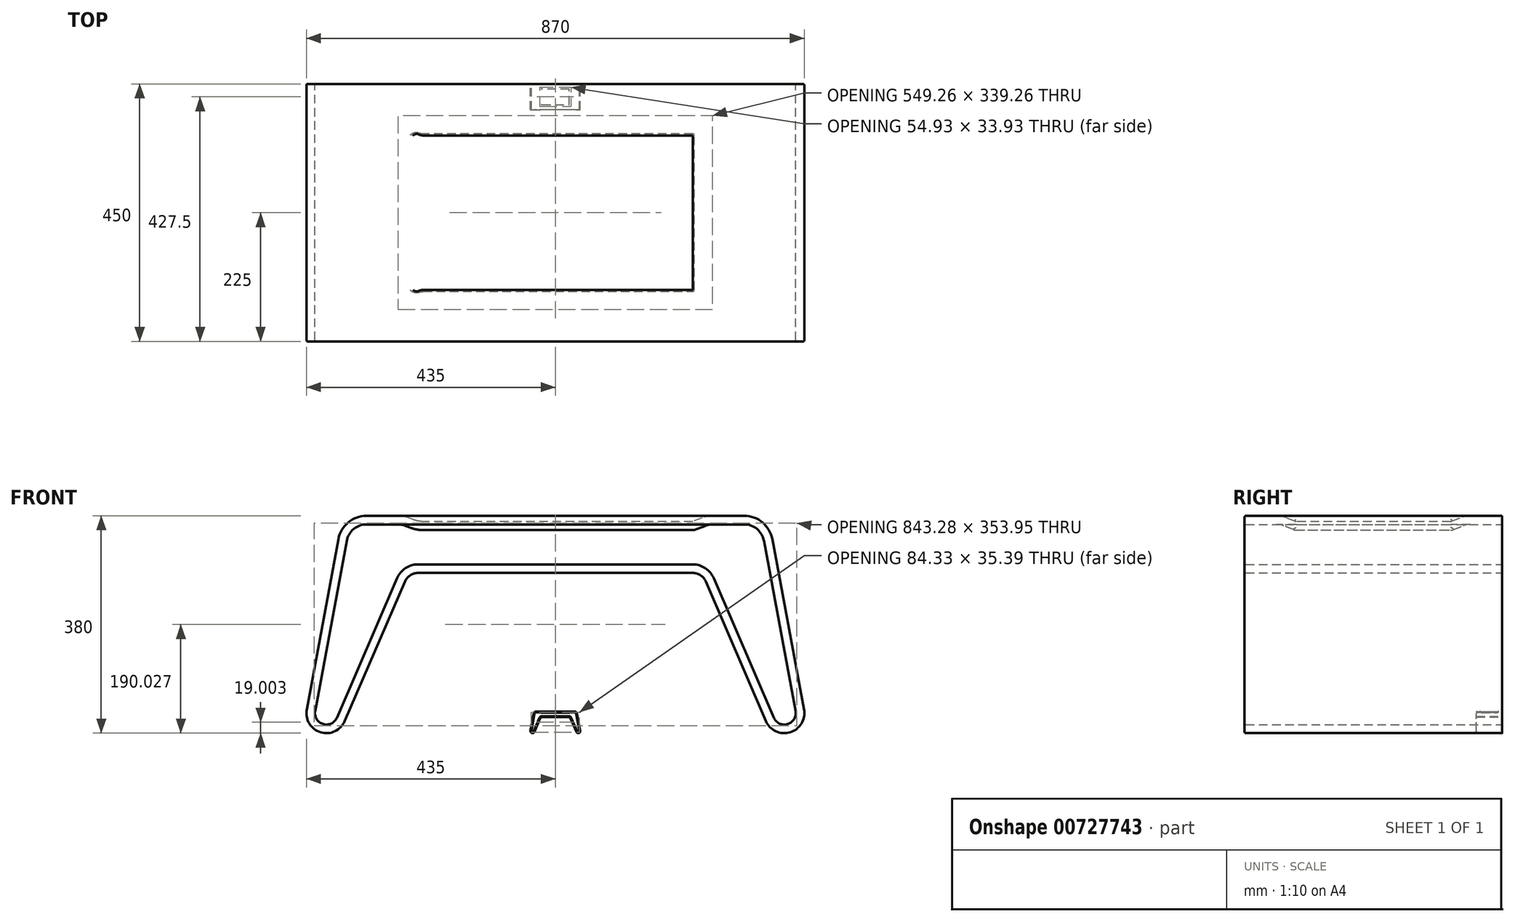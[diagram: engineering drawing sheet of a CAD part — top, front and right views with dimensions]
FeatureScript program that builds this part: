
annotation { "Feature Type Name" : "Feature", "Feature Type Description" : "" }
export const myFeature = defineFeature(function(context is Context, id is Id, definition is map)
    precondition{}
    {
        {
            var Q0;
            Q0=qCreatedBy(makeId("Front.planeOp"),FACE);
            var sketch = newSketch(context, id + "F0", { "sketchPlane" : qUnion([Q0])});
            skLineSegment(sketch, "E0", {"start": v(0, 0) * mm, "end": v(-40, 0) * mm, "construction": true});
            skLineSegment(sketch, "E1", {"start": v(0, 0) * mm, "end": v(0, 30) * mm, "construction": true});
            skArc(sketch, "E2", {"start": v(-43.44, 4.14) * mm, "mid": v(-41.02, 0.15) * mm, "end": v(-36.79, 2.12) * mm});
            skArc(sketch, "E3", {"start": v(-33, 38) * mm, "mid": v(-36.2, 36.84) * mm, "end": v(-37.92, 33.91) * mm});
            skLineSegment(sketch, "E4", {"start": v(0, 30) * mm, "end": v(0, 38) * mm, "construction": true});
            skLineSegment(sketch, "E5", {"start": v(0, 38) * mm, "end": v(-56.03, 38) * mm, "construction": true});
            skLineSegment(sketch, "E6", {"start": v(-43.44, 4.14) * mm, "end": v(-37.92, 33.91) * mm});
            skArc(sketch, "E7", {"start": v(-24, 28) * mm, "mid": v(-25.37, 27.59) * mm, "end": v(-26.3, 26.49) * mm});
            skLineSegment(sketch, "E8", {"start": v(-36.79, 2.12) * mm, "end": v(-26.3, 26.49) * mm});
            skLineSegment(sketch, "E9", {"start": v(0, 28) * mm, "end": v(-24, 28) * mm});
            skLineSegment(sketch, "E10", {"start": v(-33, 38) * mm, "end": v(0, 38) * mm});
            skLineSegment(sketch, "E11.MirrorCS", {"start": v(33, 38) * mm, "end": v(0, 38) * mm});
            skArc(sketch, "E12.MirrorCS", {"start": v(33, 38) * mm, "mid": v(36.2, 36.84) * mm, "end": v(37.92, 33.91) * mm});
            skLineSegment(sketch, "E13.MirrorCS", {"start": v(43.44, 4.14) * mm, "end": v(37.92, 33.91) * mm});
            skArc(sketch, "E14.MirrorCS", {"start": v(43.44, 4.14) * mm, "mid": v(41.02, 0.15) * mm, "end": v(36.79, 2.12) * mm});
            skLineSegment(sketch, "E15.MirrorCS", {"start": v(36.79, 2.12) * mm, "end": v(26.3, 26.49) * mm});
            skArc(sketch, "E16.MirrorCS", {"start": v(24, 28) * mm, "mid": v(25.37, 27.59) * mm, "end": v(26.3, 26.49) * mm});
            skLineSegment(sketch, "E17.MirrorCS", {"start": v(0, 28) * mm, "end": v(24, 28) * mm});
            skCircle(sketch, "E18", {"center": v(0, 11.76) * mm, "radius": 50 * mm, "construction": true});
            skSolve(sketch);
        }
        {
            var Q0;
            Q0=makeQuery(id+"F0.imprint","IMPRINT",FACE,{"disambiguationData":[TD([[makeQuery(id+"F0.imprint","IMPRINT",EDGE,{"derivedFrom":sQuery(id+"F0.wireOp",EDGE,"E2")}),1.0]])]});
            extrude(context, id + "F1", {"entities" : qUnion([Q0]), "depth" : 45 * mm, "offsetDistance" : 25 * mm});
        }
        {
            var Q0;
            Q0=makeQuery(id+"F1.opExtrude","SWEPT_FACE",FACE,{"disambiguationData":[OSD([sQuery(id+"F0.wireOp",EDGE,"E10"),sQuery(id+"F0.wireOp",EDGE,"E11.MirrorCS")])]});
            var sketch = newSketch(context, id + "F2", { "sketchPlane" : qUnion([Q0])});
            skLineSegment(sketch, "E19.0.0", {"start": v(33, 0) * mm, "end": v(-33, 0) * mm});
            skLineSegment(sketch, "E19.0.1", {"start": v(-33, 0) * mm, "end": v(-33, -45) * mm});
            skLineSegment(sketch, "E19.0.2", {"start": v(-33, -45) * mm, "end": v(33, -45) * mm});
            skLineSegment(sketch, "E19.0.3", {"start": v(33, -45) * mm, "end": v(33, 0) * mm});
            skLineSegment(sketch, "E20.0", {"start": v(-29, -9) * mm, "end": v(-29, -36) * mm});
            skLineSegment(sketch, "E20.1", {"start": v(24, -4) * mm, "end": v(-24, -4) * mm});
            skLineSegment(sketch, "E20.2", {"start": v(29, -36) * mm, "end": v(29, -9) * mm});
            skLineSegment(sketch, "E20.3", {"start": v(-24, -41) * mm, "end": v(24, -41) * mm});
            skPoint(sketch, "E21.visualSharp", {"position": v(-29, -4) * mm});
            skArc(sketch, "E21.filletArc", {"start": v(-24, -4) * mm, "mid": v(-27.54, -5.46) * mm, "end": v(-29, -9) * mm});
            skPoint(sketch, "E22.visualSharp", {"position": v(29, -4) * mm});
            skArc(sketch, "E22.filletArc", {"start": v(29, -9) * mm, "mid": v(27.54, -5.46) * mm, "end": v(24, -4) * mm});
            skPoint(sketch, "E23.visualSharp", {"position": v(29, -41) * mm});
            skArc(sketch, "E23.filletArc", {"start": v(24, -41) * mm, "mid": v(27.54, -39.54) * mm, "end": v(29, -36) * mm});
            skPoint(sketch, "E24.visualSharp", {"position": v(-29, -41) * mm});
            skArc(sketch, "E24.filletArc", {"start": v(-29, -36) * mm, "mid": v(-27.54, -39.54) * mm, "end": v(-24, -41) * mm});
            skSolve(sketch);
        }
        {
            var Q0;
            Q0=makeQuery(id+"F2.imprint","IMPRINT",FACE,{"disambiguationData":[TD([[makeQuery(id+"F2.imprint","IMPRINT",EDGE,{"derivedFrom":sQuery(id+"F2.wireOp",EDGE,"E20.0")}),1.0]])]});
            extrude(context, id + "F3", {"entities" : qUnion([Q0]), "operationType" : NewBodyOperationType.REMOVE, "oppositeDirection" : true, "depth" : 1 * mm, "offsetDistance" : 25 * mm});
        }
        {
            var Q0;
            Q0=makeQuery(id+"F3.boolean.opBoolean","COPY",FACE,{"derivedFrom":makeQuery(id+"F3.opExtrude","CAP_FACE",FACE,{"disambiguationData":[OSD([sQuery(id+"F2.wireOp",EDGE,"E20.0"),sQuery(id+"F2.wireOp",EDGE,"E20.1"),sQuery(id+"F2.wireOp",EDGE,"E20.2"),sQuery(id+"F2.wireOp",EDGE,"E20.3"),sQuery(id+"F2.wireOp",EDGE,"E21.filletArc"),sQuery(id+"F2.wireOp",EDGE,"E22.filletArc"),sQuery(id+"F2.wireOp",EDGE,"E23.filletArc"),sQuery(id+"F2.wireOp",EDGE,"E24.filletArc")])],"isStart":false})});
            chamfer(context, id + "F4", {"entities" : qUnion([Q0]), "chamferType" : ChamferType.TWO_OFFSETS, "width1" : 5 * mm, "oppositeDirection" : false, "width2" : 2 * mm, "tangentPropagation" : true});
        }
        {
            var Q0;
            Q0=makeQuery(id+"F4.opChamfer","BLEND_EDGE",EDGE,{"blendedFrom":[makeQuery(id+"F3.boolean.opBoolean","COPY",EDGE,{"derivedFrom":makeQuery(id+"F3.opExtrude","CAP_EDGE",EDGE,{"disambiguationData":[OSD([sQuery(id+"F2.wireOp",EDGE,"E20.0")])],"isStart":false})}),makeQuery(id+"F1.opExtrude","SWEPT_FACE",FACE,{"disambiguationData":[OSD([sQuery(id+"F0.wireOp",EDGE,"E10"),sQuery(id+"F0.wireOp",EDGE,"E11.MirrorCS")])]})],"blendedInto":[makeQuery(id+"F1.opExtrude","SWEPT_FACE",FACE,{"disambiguationData":[OSD([sQuery(id+"F0.wireOp",EDGE,"E10"),sQuery(id+"F0.wireOp",EDGE,"E11.MirrorCS")])]})]});
            var Q1;
            {var subQ0=sQuery(id+"F2.wireOp",EDGE,"E20.0");Q1=makeQuery(id+"F4.opChamfer","BLEND_EDGE",EDGE,{"blendedFrom":[makeQuery(id+"F3.boolean.opBoolean","COPY",EDGE,{"derivedFrom":makeQuery(id+"F3.opExtrude","CAP_EDGE",EDGE,{"disambiguationData":[OSD([subQ0])],"isStart":false})}),makeQuery(id+"F3.boolean.opBoolean","COPY",FACE,{"derivedFrom":makeQuery(id+"F3.opExtrude","CAP_FACE",FACE,{"disambiguationData":[OSD([subQ0,sQuery(id+"F2.wireOp",EDGE,"E20.1"),sQuery(id+"F2.wireOp",EDGE,"E20.2"),sQuery(id+"F2.wireOp",EDGE,"E20.3"),sQuery(id+"F2.wireOp",EDGE,"E21.filletArc"),sQuery(id+"F2.wireOp",EDGE,"E22.filletArc"),sQuery(id+"F2.wireOp",EDGE,"E23.filletArc"),sQuery(id+"F2.wireOp",EDGE,"E24.filletArc")])],"isStart":false})})],"blendedInto":[makeQuery(id+"F3.boolean.opBoolean","COPY",FACE,{"derivedFrom":makeQuery(id+"F3.opExtrude","CAP_FACE",FACE,{"disambiguationData":[OSD([subQ0,sQuery(id+"F2.wireOp",EDGE,"E20.1"),sQuery(id+"F2.wireOp",EDGE,"E20.2"),sQuery(id+"F2.wireOp",EDGE,"E20.3"),sQuery(id+"F2.wireOp",EDGE,"E21.filletArc"),sQuery(id+"F2.wireOp",EDGE,"E22.filletArc"),sQuery(id+"F2.wireOp",EDGE,"E23.filletArc"),sQuery(id+"F2.wireOp",EDGE,"E24.filletArc")])],"isStart":false})})]});}
            fillet(context, id + "F5", {"entities" : qUnion([Q0, Q1]), "radius" : 5 * mm, "tangentPropagation" : true, "allowEdgeOverflow" : false});
        }
        {
            var Q0;
            Q0=makeQuery(id+"F1.opExtrude","CAP_FACE",FACE,{"disambiguationData":[OSD([sQuery(id+"F0.wireOp",EDGE,"E2"),sQuery(id+"F0.wireOp",EDGE,"E3"),sQuery(id+"F0.wireOp",EDGE,"E6"),sQuery(id+"F0.wireOp",EDGE,"E7"),sQuery(id+"F0.wireOp",EDGE,"E8"),sQuery(id+"F0.wireOp",EDGE,"E9"),sQuery(id+"F0.wireOp",EDGE,"E10"),sQuery(id+"F0.wireOp",EDGE,"E11.MirrorCS"),sQuery(id+"F0.wireOp",EDGE,"E12.MirrorCS"),sQuery(id+"F0.wireOp",EDGE,"E13.MirrorCS"),sQuery(id+"F0.wireOp",EDGE,"E14.MirrorCS"),sQuery(id+"F0.wireOp",EDGE,"E15.MirrorCS"),sQuery(id+"F0.wireOp",EDGE,"E16.MirrorCS"),sQuery(id+"F0.wireOp",EDGE,"E17.MirrorCS")])],"isStart":false});
            var Q1;
            Q1=makeQuery(id+"F1.opExtrude","CAP_FACE",FACE,{"disambiguationData":[OSD([sQuery(id+"F0.wireOp",EDGE,"E2"),sQuery(id+"F0.wireOp",EDGE,"E3"),sQuery(id+"F0.wireOp",EDGE,"E6"),sQuery(id+"F0.wireOp",EDGE,"E7"),sQuery(id+"F0.wireOp",EDGE,"E8"),sQuery(id+"F0.wireOp",EDGE,"E9"),sQuery(id+"F0.wireOp",EDGE,"E10"),sQuery(id+"F0.wireOp",EDGE,"E11.MirrorCS"),sQuery(id+"F0.wireOp",EDGE,"E12.MirrorCS"),sQuery(id+"F0.wireOp",EDGE,"E13.MirrorCS"),sQuery(id+"F0.wireOp",EDGE,"E14.MirrorCS"),sQuery(id+"F0.wireOp",EDGE,"E15.MirrorCS"),sQuery(id+"F0.wireOp",EDGE,"E16.MirrorCS"),sQuery(id+"F0.wireOp",EDGE,"E17.MirrorCS")])],"isStart":true});
            shell(context, id + "F6", {"entities" : qUnion([Q0, Q1]), "thickness" : 1.5 * mm});
        }
        {
            var Q0;
            Q0=makeQuery(id+"F1.opExtrude","CAP_FACE",FACE,{"disambiguationData":[OSD([sQuery(id+"F0.wireOp",EDGE,"E2"),sQuery(id+"F0.wireOp",EDGE,"E3"),sQuery(id+"F0.wireOp",EDGE,"E6"),sQuery(id+"F0.wireOp",EDGE,"E7"),sQuery(id+"F0.wireOp",EDGE,"E8"),sQuery(id+"F0.wireOp",EDGE,"E9"),sQuery(id+"F0.wireOp",EDGE,"E10"),sQuery(id+"F0.wireOp",EDGE,"E11.MirrorCS"),sQuery(id+"F0.wireOp",EDGE,"E12.MirrorCS"),sQuery(id+"F0.wireOp",EDGE,"E13.MirrorCS"),sQuery(id+"F0.wireOp",EDGE,"E14.MirrorCS"),sQuery(id+"F0.wireOp",EDGE,"E15.MirrorCS"),sQuery(id+"F0.wireOp",EDGE,"E16.MirrorCS"),sQuery(id+"F0.wireOp",EDGE,"E17.MirrorCS")])],"isStart":false});
            var Q1;
            Q1=makeQuery(id+"F1.opExtrude","CAP_FACE",FACE,{"disambiguationData":[OSD([sQuery(id+"F0.wireOp",EDGE,"E2"),sQuery(id+"F0.wireOp",EDGE,"E3"),sQuery(id+"F0.wireOp",EDGE,"E6"),sQuery(id+"F0.wireOp",EDGE,"E7"),sQuery(id+"F0.wireOp",EDGE,"E8"),sQuery(id+"F0.wireOp",EDGE,"E9"),sQuery(id+"F0.wireOp",EDGE,"E10"),sQuery(id+"F0.wireOp",EDGE,"E11.MirrorCS"),sQuery(id+"F0.wireOp",EDGE,"E12.MirrorCS"),sQuery(id+"F0.wireOp",EDGE,"E13.MirrorCS"),sQuery(id+"F0.wireOp",EDGE,"E14.MirrorCS"),sQuery(id+"F0.wireOp",EDGE,"E15.MirrorCS"),sQuery(id+"F0.wireOp",EDGE,"E16.MirrorCS"),sQuery(id+"F0.wireOp",EDGE,"E17.MirrorCS")])],"isStart":true});
            fillet(context, id + "F7", {"entities" : qUnion([Q0, Q1]), "radius" : 0.2 * mm, "tangentPropagation" : true, "allowEdgeOverflow" : false});
        }
        {
            var Q0;
            Q0=makeQuery(id+"F1.opExtrude","SWEPT_BODY",BODY,{"disambiguationData":[OSD([sQuery(id+"F0.wireOp",EDGE,"E2"),sQuery(id+"F0.wireOp",EDGE,"E3"),sQuery(id+"F0.wireOp",EDGE,"E6"),sQuery(id+"F0.wireOp",EDGE,"E7"),sQuery(id+"F0.wireOp",EDGE,"E8"),sQuery(id+"F0.wireOp",EDGE,"E9"),sQuery(id+"F0.wireOp",EDGE,"E10"),sQuery(id+"F0.wireOp",EDGE,"E11.MirrorCS"),sQuery(id+"F0.wireOp",EDGE,"E12.MirrorCS"),sQuery(id+"F0.wireOp",EDGE,"E13.MirrorCS"),sQuery(id+"F0.wireOp",EDGE,"E14.MirrorCS"),sQuery(id+"F0.wireOp",EDGE,"E15.MirrorCS"),sQuery(id+"F0.wireOp",EDGE,"E16.MirrorCS"),sQuery(id+"F0.wireOp",EDGE,"E17.MirrorCS")])]});
            var Q1;
            Q1=qCreatedBy(makeId("Origin.pointOp"),VERTEX);
            transform(context, id + "F8", {"entities" : qUnion([Q0]), "transformType" : TransformType.SCALE_UNIFORMLY, "scale" : 10, "scalePoint" : qUnion([Q1]), "makeCopy" : true});
        }
    });
